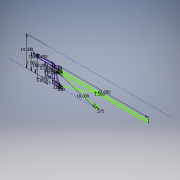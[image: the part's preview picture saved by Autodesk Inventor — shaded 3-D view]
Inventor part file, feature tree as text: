
AUTODESK INVENTOR PART (.ipt)
format: ipt  version: 2017 SP1 (Build 210196100, 196)  size: 120,320 bytes
history: native  units: in
note: dims shown in document units (in); Inventor stores cm internally (conversion verified against a paired STEP export)
features: sketch x1
ambient origin geometry x8: Origin, YZ Plane, XZ Plane, XY Plane, X Axis, Y Axis, Z Axis, Center Point
feature tree (1):
  sketch  "Sketch1"  dims[d0=5.0in d1=2.0in d3=1.0in d4=5.0in d5=7.5in d7=8.25in d10=1.25in d11=3.25in d12=1.0in d13=42.0in d15=0.375in d16=14.0in d17=0.125in d18=1.5in d19=3.0in d21=8.0in d22=0.0in d23=18.0in d24=0.5in d25=0.125in d26=0.5in d27=0.75in d28=1.25in]
